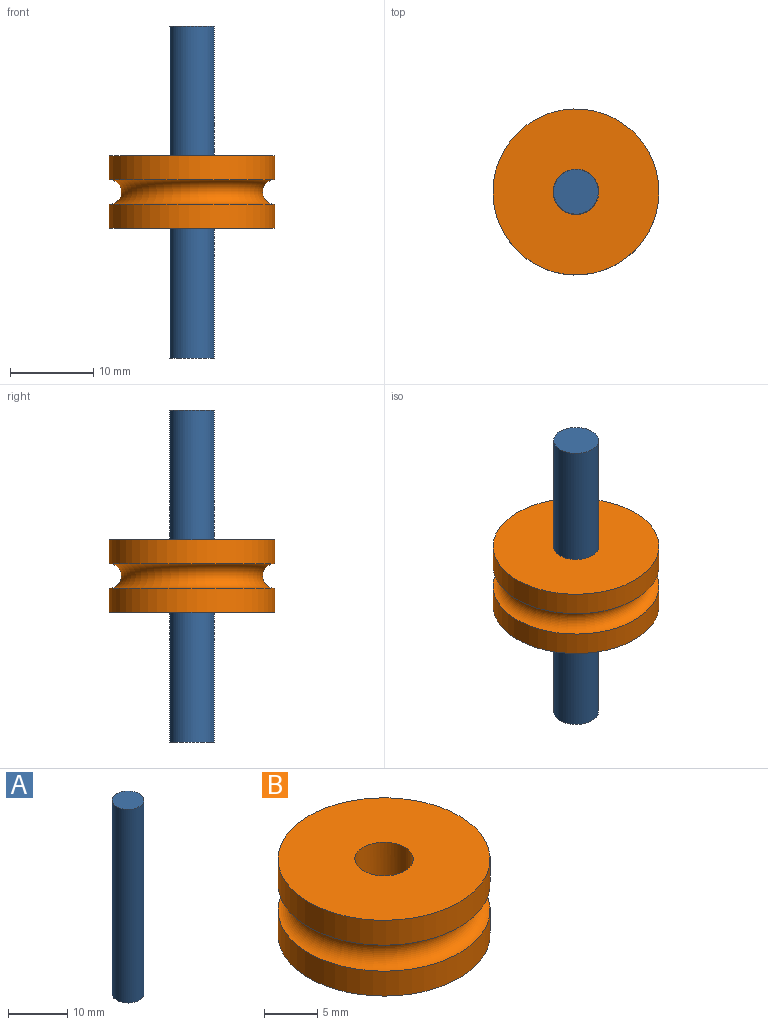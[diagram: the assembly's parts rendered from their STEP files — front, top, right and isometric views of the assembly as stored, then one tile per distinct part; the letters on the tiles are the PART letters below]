
ASSEMBLY  parts=2 mates=1
PART A: 3 faces, bbox 5.4x5.4x40 mm
  f0: plane 5.4x5.4mm, normal (0,0,1), area 22.9mm2, adj f1
  f1: cylinder r=2.7mm len=40mm, axis (0,0,1), area 678.6mm2, adj f0,f2
  f2: plane 5.4x5.4mm, normal (0,0,-1), area 22.9mm2, adj f1
PART B: 6 faces, bbox 24x24x8.8 mm
  f0: plane 20x20mm, normal (0,0,1), area 290.4mm2, adj f1,f5
  f1: cylinder r=10mm len=20mm, axis (0,0,1), area 180.6mm2, adj f0,f2
  f2: torus R=10mm, axis (0,0,1), area 267.8mm2, adj f1,f3
  f3: cylinder r=10mm len=20mm, axis (0,0,1), area 180.6mm2, adj f2,f4
  f4: plane 20x20mm, normal (0,0,-1), area 290.4mm2, adj f3,f5
  f5: cylinder r=2.75mm len=8.75mm, axis (0,0,-1), area 151.2mm2, adj f0,f4
PLACE A t=(-11.42,-45.23,7.59)mm
PLACE B t=(-13.75,-45.23,6.05)mm
MATE revolute A.f1 <-> B.f5  axis (0,0,1) through (-14.73,-45.23,3.05)mm
